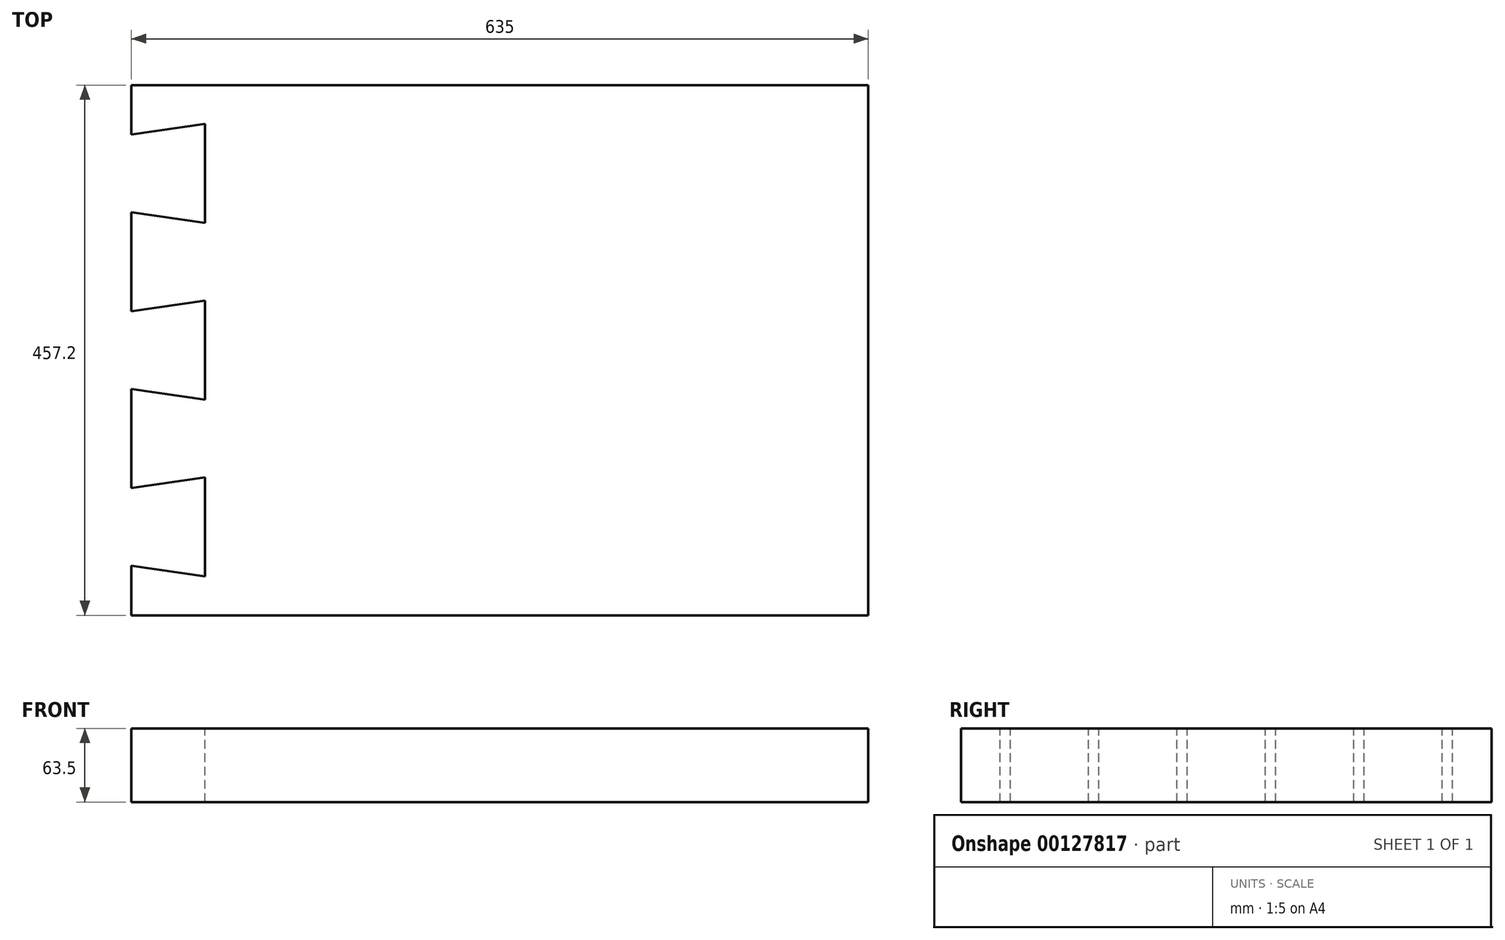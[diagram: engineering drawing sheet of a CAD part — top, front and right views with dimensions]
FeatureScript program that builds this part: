
annotation { "Feature Type Name" : "Feature", "Feature Type Description" : "" }
export const myFeature = defineFeature(function(context is Context, id is Id, definition is map)
    precondition{}
    {
        {
            var Q0;
            Q0=qCreatedBy(makeId("Top.planeOp"),FACE);
            var sketch = newSketch(context, id + "F0", { "sketchPlane" : qUnion([Q0])});
            skLineSegment(sketch, "E0.bottom", {"start": v(0, 0) * mm, "end": v(635, 0) * mm});
            skLineSegment(sketch, "E0.top", {"start": v(0, -457.2) * mm, "end": v(635, -457.2) * mm});
            skLineSegment(sketch, "E0.left", {"start": v(0, 0) * mm, "end": v(0, -457.2) * mm});
            skLineSegment(sketch, "E0.right", {"start": v(635, 0) * mm, "end": v(635, -457.2) * mm});
            skSolve(sketch);
        }
        {
            var Q0;
            Q0 = qSketchRegion(id + "F0", true);
            extrude(context, id + "F1", {"entities" : qUnion([Q0]), "oppositeDirection" : true, "depth" : 63.5 * mm});
        }
        {
            var Q0;
            Q0=qCreatedBy(makeId("Top.planeOp"),FACE);
            var sketch = newSketch(context, id + "F2", { "sketchPlane" : qUnion([Q0])});
            skLineSegment(sketch, "E1", {"start": v(0, -42.56) * mm, "end": v(63.5, -33.64) * mm});
            skLineSegment(sketch, "E2", {"start": v(63.5, -33.64) * mm, "end": v(63.5, -118.76) * mm});
            skLineSegment(sketch, "E3", {"start": v(63.5, -118.76) * mm, "end": v(0, -109.84) * mm});
            skLineSegment(sketch, "E4", {"start": v(0, -109.84) * mm, "end": v(0, -42.56) * mm});
            skLineSegment(sketch, "E5", {"start": v(63.5, -118.76) * mm, "end": v(63.5, -186.04) * mm, "construction": true});
            skLineSegment(sketch, "E6", {"start": v(0, -194.96) * mm, "end": v(63.5, -186.04) * mm});
            skLineSegment(sketch, "E7", {"start": v(63.5, -271.16) * mm, "end": v(63.5, -186.04) * mm});
            skLineSegment(sketch, "E8", {"start": v(63.5, -271.16) * mm, "end": v(0, -262.24) * mm});
            skLineSegment(sketch, "E9", {"start": v(0, -262.24) * mm, "end": v(0, -194.96) * mm});
            skLineSegment(sketch, "E10", {"start": v(0, -347.36) * mm, "end": v(63.5, -338.44) * mm});
            skLineSegment(sketch, "E11", {"start": v(63.5, -338.44) * mm, "end": v(63.5, -423.56) * mm});
            skLineSegment(sketch, "E12", {"start": v(63.5, -423.56) * mm, "end": v(0, -414.64) * mm});
            skLineSegment(sketch, "E13", {"start": v(0, -414.64) * mm, "end": v(0, -347.36) * mm});
            skLineSegment(sketch, "E14", {"start": v(63.5, -271.16) * mm, "end": v(63.5, -338.44) * mm, "construction": true});
            skLineSegment(sketch, "E15", {"start": v(63.5, -33.64) * mm, "end": v(63.5, 0) * mm, "construction": true});
            skLineSegment(sketch, "E16", {"start": v(63.5, -423.56) * mm, "end": v(63.5, -457.2) * mm, "construction": true});
            skLineSegment(sketch, "E17", {"start": v(63.5, -118.76) * mm, "end": v(63.5, -152.4) * mm, "construction": true});
            skLineSegment(sketch, "E18", {"start": v(63.5, -152.4) * mm, "end": v(63.5, -186.04) * mm, "construction": true});
            skSolve(sketch);
        }
        {
            var Q0;
            Q0 = qSketchRegion(id + "F2", true);
            extrude(context, id + "F3", {"entities" : qUnion([Q0]), "operationType" : NewBodyOperationType.REMOVE, "endBound" : BoundingType.THROUGH_ALL, "oppositeDirection" : true, "depth" : 25.4 * mm});
        }
        {
            var Q0;
            Q0=makeQuery(id+"F1.opExtrude","SWEPT_FACE",FACE,{"disambiguationData":[OSD([sQuery(id+"F0.wireOp",EDGE,"E0.right")])]});
            var Q1;
            Q1=qCreatedBy(makeId("Right.planeOp"),FACE);
            cPlane(context, id + "F4", {"entities" : qUnion([Q0, Q1]), "cplaneType" : CPlaneType.MID_PLANE, "offset" : 25.4 * mm, "width" : 152.4 * mm, "height" : 152.4 * mm});
        }
    });
